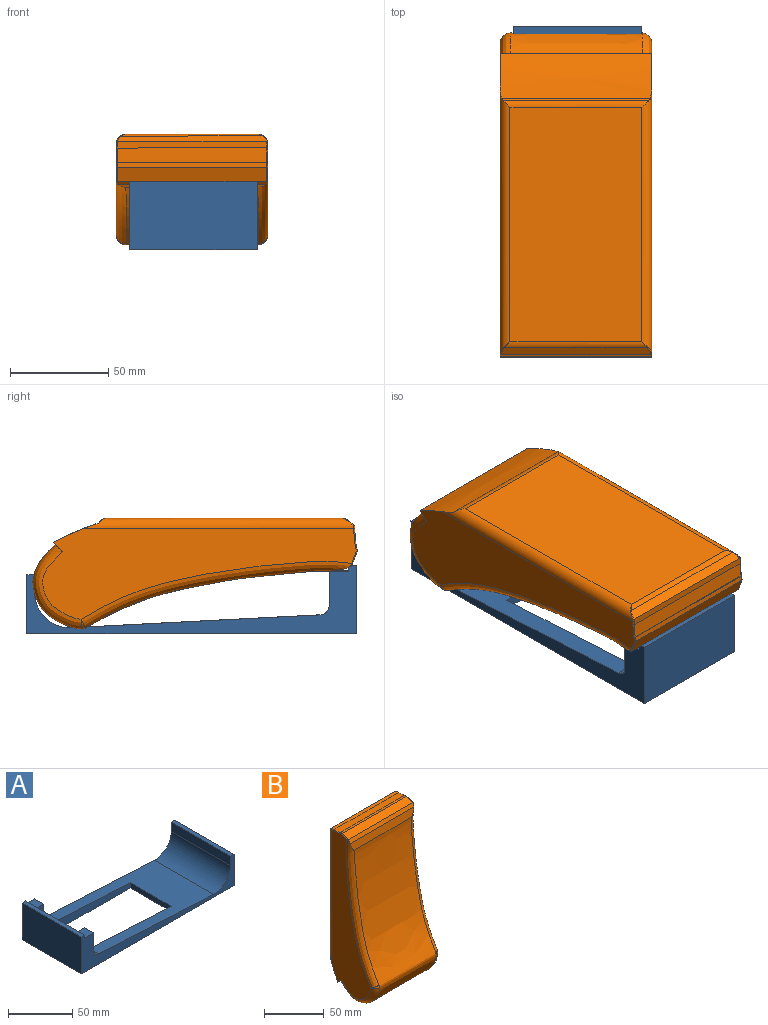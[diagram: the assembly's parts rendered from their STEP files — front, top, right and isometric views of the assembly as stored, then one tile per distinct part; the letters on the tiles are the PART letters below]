
ASSEMBLY  parts=2 mates=1
PART A: 20 faces, bbox 168x65x35 mm
  f0: plane 126.47x65mm, normal (0.05,0,1), area 4167mm2, adj f1,f2,f3,f4,f6,f17,f18,f19
  f1: plane 104.95x32mm, normal (0,-1,0), area 1033.3mm2, adj f0,f2,f7,f10,f13,f14,f19
  f2: plane 45x5.01mm, normal (-1,0,0), area 225.3mm2, adj f0,f1,f3,f7
  f3: plane 104.95x32mm, normal (0,1,0), area 1033.3mm2, adj f0,f2,f7,f10,f15,f16,f18
  f4: plane 168x35mm, normal (0,-1,0), area 1567.7mm2, adj f0,f5,f7,f8,f9,f10,f11,f12
  f5: plane 65x30mm, normal (1,0,0), area 1950mm2, adj f4,f6,f7,f9
  f6: plane 168x35mm, normal (0,1,0), area 1567.7mm2, adj f0,f5,f7,f8,f9,f10,f11,f12
  f7: plane 168x65mm, normal (0,0,-1), area 6197.5mm2, adj f1,f2,f3,f4,f5,f6,f10,f11
  f8: plane 65x9.03mm, normal (-1,0,0), area 586.8mm2, adj f4,f6,f9,f17
  f9: plane 65x4mm, normal (0,0,1), area 260mm2, adj f4,f5,f6,f8
  f10: plane 65x35mm, normal (1,0,0), area 1635mm2, adj f1,f3,f4,f6,f7,f12,f14,f16
  f11: plane 65x35mm, normal (-1,0,0), area 2275mm2, adj f4,f6,f7,f12
  f12: plane 65x4mm, normal (0,0,1), area 260mm2, adj f4,f6,f10,f11
  f13: plane 17.33x10mm, normal (1,0,0), area 173.3mm2, adj f1,f6,f14,f19
  f14: plane 10x10mm, normal (0,0,1), area 100mm2, adj f1,f6,f10,f13
  f15: plane 17.33x10mm, normal (1,0,0), area 173.3mm2, adj f3,f4,f16,f18
  f16: plane 10x10mm, normal (0,0,1), area 100mm2, adj f3,f4,f10,f15
  f17: cylinder r=17.87mm len=65mm, axis (0,1,0), area 1884.1mm2, adj f0,f4,f6,f8
  f18: cylinder r=5mm len=10mm, axis (0,-1,0), area 76mm2, adj f0,f3,f4,f15
  f19: cylinder r=5mm len=10mm, axis (0,-1,0), area 76mm2, adj f0,f1,f6,f13
PART B: 43 faces, bbox 77.5x56.6x197.6 mm
  f0: plane 76.01x1.17mm, normal (0,0.71,-0.71), area 117.7mm2, adj f12,f16,f17,f18
  f1: plane 119.29x67.2mm, normal (0,1,0), area 8016.3mm2, adj f15,f16,f17,f18
  f2: plane 76x3.76mm, normal (0,0.81,0.58), area 346.1mm2, adj f3,f15,f31,f32,f35,f36
  f3: plane 76.2x3.38mm, normal (0,0,1), area 257.4mm2, adj f2,f4,f30,f31,f36,f37
  f4: plane 76.2x7.3mm, normal (0,0.09,1), area 559.1mm2, adj f3,f5,f29,f38
  f5: plane 76.2x0.27mm, normal (0,1,-0.09), area 20.6mm2, adj f4,f6,f28,f39
  f6: plane 76.2x2.55mm, normal (0,0.09,1), area 195.3mm2, adj f5,f7,f27,f40
  f7: plane 76.2x7.35mm, normal (0,-0.35,0.94), area 598.5mm2, adj f6,f8,f25,f26,f41,f42
  f8: plane 76.94x3.71mm, normal (0,-0.91,0.42), area 293.3mm2, adj f7,f9,f19,f22,f25,f42
  f9: plane 74.9x7.97mm, normal (0,-0.99,0.13), area 583.4mm2, adj f8,f10,f19,f22
  f10: extruded ~150.84x67.2mm, area 12887.8mm2, adj f9,f11,f19,f20,f21,f22,f23,f24
  f11: plane 77.37x4.92mm, normal (0,-0.69,-0.73), area 129.9mm2, adj f10,f12,f13,f14,f21,f24
  f12: extruded ~77.2x22.93mm, area 1918.9mm2, adj f0,f11,f13,f14,f16,f17
  f13: plane 159.59x46.46mm, normal (1,0,0), area 4127.6mm2, adj f11,f12,f16,f22,f24,f26,f27,f28
  f14: plane 159.59x46.46mm, normal (-1,0,0), area 4127.6mm2, adj f11,f12,f17,f19,f21,f37,f38,f39
  f15: cylinder r=5mm len=72.46mm, axis (-1,0,0), area 218.1mm2, adj f1,f2,f33,f34
  f16: cylinder r=5mm len=136.96mm, axis (0,0,-1), area 997.1mm2, adj f0,f1,f12,f13,f18,f31,f32,f33
  f17: cylinder r=5mm len=136.96mm, axis (0,0,1), area 997.1mm2, adj f0,f1,f12,f14,f18,f34,f35,f36
  f18: cylinder r=5mm len=74.29mm, axis (1,0,0), area 278.8mm2, adj f0,f1,f16,f17
  f19: bspline ~173.13x34.26mm, area 1067.1mm2, adj f8,f9,f10,f14,f20,f42
  f20: bspline ~5x5mm, area 6.9mm2, adj f10,f19,f21
  f21: bspline ~43.67x25.12mm, area 440.5mm2, adj f10,f11,f14,f20
  f22: bspline ~173.13x34.26mm, area 1067.1mm2, adj f8,f9,f10,f13,f23,f25
  f23: bspline ~5x5mm, area 6.9mm2, adj f10,f22,f24
  f24: bspline ~43.67x25.12mm, area 440.5mm2, adj f10,f11,f13,f23
  f25: bspline ~2.76x1.4mm, area 1.1mm2, adj f7,f8,f22,f26
  f26: cylinder r=0.5mm len=6.46mm, axis (0,0.94,0.35), area 5.2mm2, adj f7,f13,f25,f27
  f27: cylinder r=0.5mm len=2.6mm, axis (0,1,-0.09), area 1.8mm2, adj f6,f13,f26,f28
  f28: cylinder r=0.5mm len=0.81mm, axis (0,-0.09,-1), area 0.2mm2, adj f5,f13,f27,f29
  f29: cylinder r=0.5mm len=7.87mm, axis (0,1,-0.09), area 6mm2, adj f4,f13,f28,f30
  f30: cylinder r=0.5mm len=2.06mm, axis (0,1,0), area 1.6mm2, adj f3,f13,f29,f31
  f31: torus R=4.5mm, axis (0,0,-1), area 1mm2, adj f2,f3,f16,f30,f32
  f32: bspline ~4.04x3.04mm, area 2.8mm2, adj f2,f16,f31,f33
  f33: bspline ~3.3x3.3mm, area 0.6mm2, adj f15,f16,f32
  f34: bspline ~3.3x3.3mm, area 0.6mm2, adj f15,f17,f35
  f35: bspline ~4.04x3.04mm, area 2.8mm2, adj f2,f17,f34,f36
  f36: torus R=4.5mm, axis (0,0,-1), area 1mm2, adj f2,f3,f17,f35,f37
  f37: cylinder r=0.5mm len=2.06mm, axis (0,-1,0), area 1.6mm2, adj f3,f14,f36,f38
  f38: cylinder r=0.5mm len=7.87mm, axis (0,-1,0.09), area 6mm2, adj f4,f14,f37,f39
  f39: cylinder r=0.5mm len=0.81mm, axis (0,0.09,1), area 0.2mm2, adj f5,f14,f38,f40
  f40: cylinder r=0.5mm len=2.6mm, axis (0,-1,0.09), area 1.8mm2, adj f6,f14,f39,f41
  f41: cylinder r=0.5mm len=6.46mm, axis (0,-0.94,-0.35), area 5.2mm2, adj f7,f14,f40,f42
  f42: bspline ~2.76x1.4mm, area 1.1mm2, adj f7,f8,f19,f41
PLACE A rot(axis=(0,0,1),90deg) t=(-35.33,13.87,130.51)mm
PLACE B rot(axis=(1,0,0),90deg) t=(-36.05,12.23,161.85)mm
MATE parallel A.f7 <-> B.f1  axis (0,0,-1) through (-35.32,97.87,130.51)mm
